# Revit family: Side Wall Grille-Large-Rectangular Connection-Return & Extract
name_source: partatom
category: Air Terminals
revit_build: Autodesk Revit MEP 2013 (Build: 20130531_2115(x64)
units: mm (PartAtom-declared; Revit-internal decimal feet)

## types (10) — shared parameters
Colour = BY ARCHITECT
Damper Material = S.S.
Flange Thk = 20 mm
Flange Width = 25 mm
Manufacturer = EH PRICE
Material = POWDER COATED AC
Model = 7200

## per-type parameters (varying)
| type | Air Terminal Type | Grille Height | No.of Fins | Slot |
| Side Wall Grille-Supply-150mm | DOUBLE DEFLECTION TYPE (SUPPLY) | 250 mm | 9 | Grille |
| Side Wall Grille-Supply-100mm | DOUBLE DEFLECTION GRILLE (SUPPLY) | 100 mm | 3 | <By Category> |
| Side Wall Grille-Supply-200mm | DOUBLE DEFLECTION GRILLE (SUPPLY) | 200 mm | 7 | <By Category> |
| Side Wall Grille-Supply-250mm | DOUBLE DEFLECTION GRILLE (SUPPLY) | 250 mm | 9 | <By Category> |
| Side Wall Grille-Supply-300mm | DOUBLE DEFLECTION TYPE (SUPPLY) | 250 mm | 9 | Grille |
| Side Wall Grille-Supply-900mm | DOUBLE DEFLECTION TYPE (SUPPLY) | 900 mm | 35 | <By Category> |
| Side Wall Grille-Supply-600 | DOUBLE DEFLECTION TYPE (SUPPLY) | 600 mm | 23 | <By Category> |
| Side Wall Grille-Supply-800mm | DOUBLE DEFLECTION TYPE (SUPPLY) | 800 mm | 31 | <By Category> |
| Side Wall Grille-Supply-1000mm | DOUBLE DEFLECTION TYPE (SUPPLY) | 1000 mm | 39 | <By Category> |
| Side Wall Grille-Supply | DOUBLE DEFLECTION GRILLE (SUPPLY) | 150 mm | 5 | <By Category> |

## geometry (parser evidence)
native form markers: Blend x12, Sweep x5
no freeform markers — native parametric forms only
